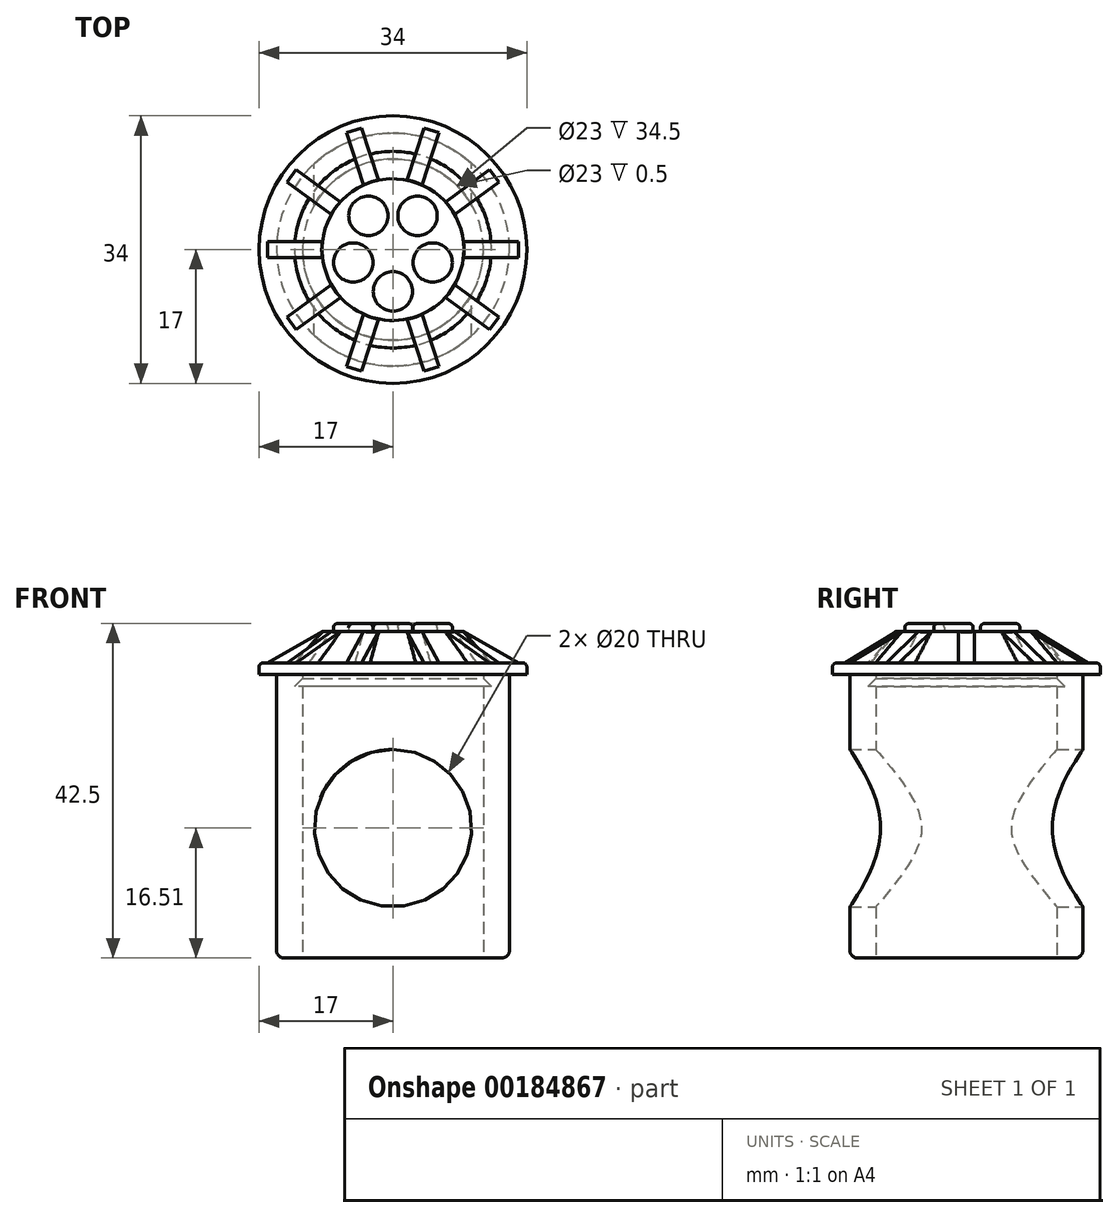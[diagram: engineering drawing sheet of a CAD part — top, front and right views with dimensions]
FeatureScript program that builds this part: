
annotation { "Feature Type Name" : "Feature", "Feature Type Description" : "" }
export const myFeature = defineFeature(function(context is Context, id is Id, definition is map)
    precondition{}
    {
        {
            var Q0;
            Q0=qCreatedBy(makeId("Top.planeOp"),FACE);
            var sketch = newSketch(context, id + "F0", { "sketchPlane" : qUnion([Q0])});
            skCircle(sketch, "E0", {"center": v(0, 0) * mm, "radius": 14.8 * mm});
            skCircle(sketch, "E1", {"center": v(0, 0) * mm, "radius": 11.5 * mm});
            skSolve(sketch);
        }
        {
            var Q0;
            Q0=qSketchRegion(id+"F0",true);
            extrude(context, id + "F1", {"entities" : qUnion([Q0]), "endBound" : BoundingType.SYMMETRIC, "depth" : 36 * mm});
        }
        {
            var Q0;
            Q0=makeQuery(id+"F1.opExtrude","SWEPT_BODY",BODY,{"disambiguationData":[OSD([sQuery(id+"F0.wireOp",EDGE,"E0")])]});
            transform(context, id + "F2", {"entities" : qUnion([Q0]), "transformType" : TransformType.TRANSLATION_3D, "dx" : 0 * mm, "dy" : 0 * mm, "dz" : -23.5 * mm, "makeCopy" : false});
        }
        {
            var Q0;
            Q0=qCreatedBy(makeId("Top.planeOp"),FACE);
            var sketch = newSketch(context, id + "F3", { "sketchPlane" : qUnion([Q0])});
            skCircle(sketch, "E2", {"center": v(0, 0) * mm, "radius": 9 * mm});
            skSolve(sketch);
        }
        {
            var Q0;
            Q0=qSketchRegion(id+"F3",true);
            extrude(context, id + "F4", {"entities" : qUnion([Q0]), "depth" : 4 * mm});
        }
        {
            var Q0;
            Q0=qCreatedBy(makeId("Front.planeOp"),FACE);
            var sketch = newSketch(context, id + "F5", { "sketchPlane" : qUnion([Q0])});
            skLineSegment(sketch, "E3", {"start": v(8.92, 4) * mm, "end": v(8.92, 0) * mm});
            skLineSegment(sketch, "E4", {"start": v(8.92, 0) * mm, "end": v(15.92, 0) * mm});
            skLineSegment(sketch, "E5", {"start": v(15.92, 0) * mm, "end": v(8.92, 4) * mm});
            skSolve(sketch);
        }
        {
            var Q0;
            Q0=qSketchRegion(id+"F5",true);
            extrude(context, id + "F6", {"entities" : qUnion([Q0]), "endBound" : BoundingType.SYMMETRIC, "depth" : 2 * mm});
        }
        {
            var Q0;
            Q0=makeQuery(id+"F6.opExtrude","SWEPT_BODY",BODY,{"disambiguationData":[OSD([sQuery(id+"F5.wireOp",EDGE,"E3"),sQuery(id+"F5.wireOp",EDGE,"E4"),sQuery(id+"F5.wireOp",EDGE,"E5")])]});
            var Q1;
            Q1=makeQuery(id+"F4.opExtrude","SWEPT_FACE",FACE,{"disambiguationData":[OSD([sQuery(id+"F3.wireOp",EDGE,"E2")])]});
            circularPattern(context, id + "F7", {"entities" : qUnion([Q0]), "axis" : qUnion([Q1]), "angle" : 36 * degree, "instanceCount" : 10});
        }
        {
            var Q0;
            Q0=qCreatedBy(makeId("Front.planeOp"),FACE);
            var sketch = newSketch(context, id + "F8", { "sketchPlane" : qUnion([Q0])});
            skLineSegment(sketch, "E6", {"start": v(8.98, 0) * mm, "end": v(8.98, 4) * mm});
            skLineSegment(sketch, "E7", {"start": v(8.98, 4) * mm, "end": v(12.48, 0) * mm});
            skLineSegment(sketch, "E8", {"start": v(12.48, 0) * mm, "end": v(8.98, 0) * mm});
            skSolve(sketch);
        }
        {
            var Q0;
            Q0=qSketchRegion(id+"F8",true);
            var Q1;
            Q1=makeQuery(id+"F4.opExtrude","SWEPT_FACE",FACE,{"disambiguationData":[OSD([sQuery(id+"F3.wireOp",EDGE,"E2")])]});
            revolve(context, id + "F9", {"operationType" : NewBodyOperationType.ADD, "entities" : qUnion([Q0]), "axis" : qUnion([Q1]), "revolveType" : RevolveType.FULL});
        }
        {
            var Q0;
            Q0=makeQuery(id+"F4.opExtrude","SWEPT_BODY",BODY,{"disambiguationData":[OSD([sQuery(id+"F3.wireOp",EDGE,"E2")])]});
            var Q1;
            Q1=makeQuery(id+"F6.opExtrude","SWEPT_BODY",BODY,{"disambiguationData":[OSD([sQuery(id+"F5.wireOp",EDGE,"E3"),sQuery(id+"F5.wireOp",EDGE,"E4"),sQuery(id+"F5.wireOp",EDGE,"E5")])]});
            var Q2;
            Q2=makeQuery(id+"F7.opPattern","COPY",BODY,{"derivedFrom":makeQuery(id+"F6.opExtrude","SWEPT_BODY",BODY,{"disambiguationData":[OSD([sQuery(id+"F5.wireOp",EDGE,"E3"),sQuery(id+"F5.wireOp",EDGE,"E4"),sQuery(id+"F5.wireOp",EDGE,"E5")])]}),"instanceName":"1"});
            var Q3;
            Q3=makeQuery(id+"F7.opPattern","COPY",BODY,{"derivedFrom":makeQuery(id+"F6.opExtrude","SWEPT_BODY",BODY,{"disambiguationData":[OSD([sQuery(id+"F5.wireOp",EDGE,"E3"),sQuery(id+"F5.wireOp",EDGE,"E4"),sQuery(id+"F5.wireOp",EDGE,"E5")])]}),"instanceName":"2"});
            var Q4;
            Q4=makeQuery(id+"F7.opPattern","COPY",BODY,{"derivedFrom":makeQuery(id+"F6.opExtrude","SWEPT_BODY",BODY,{"disambiguationData":[OSD([sQuery(id+"F5.wireOp",EDGE,"E3"),sQuery(id+"F5.wireOp",EDGE,"E4"),sQuery(id+"F5.wireOp",EDGE,"E5")])]}),"instanceName":"3"});
            var Q5;
            Q5=makeQuery(id+"F7.opPattern","COPY",BODY,{"derivedFrom":makeQuery(id+"F6.opExtrude","SWEPT_BODY",BODY,{"disambiguationData":[OSD([sQuery(id+"F5.wireOp",EDGE,"E3"),sQuery(id+"F5.wireOp",EDGE,"E4"),sQuery(id+"F5.wireOp",EDGE,"E5")])]}),"instanceName":"4"});
            var Q6;
            Q6=makeQuery(id+"F7.opPattern","COPY",BODY,{"derivedFrom":makeQuery(id+"F6.opExtrude","SWEPT_BODY",BODY,{"disambiguationData":[OSD([sQuery(id+"F5.wireOp",EDGE,"E3"),sQuery(id+"F5.wireOp",EDGE,"E4"),sQuery(id+"F5.wireOp",EDGE,"E5")])]}),"instanceName":"5"});
            var Q7;
            Q7=makeQuery(id+"F7.opPattern","COPY",BODY,{"derivedFrom":makeQuery(id+"F6.opExtrude","SWEPT_BODY",BODY,{"disambiguationData":[OSD([sQuery(id+"F5.wireOp",EDGE,"E3"),sQuery(id+"F5.wireOp",EDGE,"E4"),sQuery(id+"F5.wireOp",EDGE,"E5")])]}),"instanceName":"6"});
            var Q8;
            Q8=makeQuery(id+"F7.opPattern","COPY",BODY,{"derivedFrom":makeQuery(id+"F6.opExtrude","SWEPT_BODY",BODY,{"disambiguationData":[OSD([sQuery(id+"F5.wireOp",EDGE,"E3"),sQuery(id+"F5.wireOp",EDGE,"E4"),sQuery(id+"F5.wireOp",EDGE,"E5")])]}),"instanceName":"7"});
            var Q9;
            Q9=makeQuery(id+"F7.opPattern","COPY",BODY,{"derivedFrom":makeQuery(id+"F6.opExtrude","SWEPT_BODY",BODY,{"disambiguationData":[OSD([sQuery(id+"F5.wireOp",EDGE,"E3"),sQuery(id+"F5.wireOp",EDGE,"E4"),sQuery(id+"F5.wireOp",EDGE,"E5")])]}),"instanceName":"8"});
            var Q10;
            Q10=makeQuery(id+"F7.opPattern","COPY",BODY,{"derivedFrom":makeQuery(id+"F6.opExtrude","SWEPT_BODY",BODY,{"disambiguationData":[OSD([sQuery(id+"F5.wireOp",EDGE,"E3"),sQuery(id+"F5.wireOp",EDGE,"E4"),sQuery(id+"F5.wireOp",EDGE,"E5")])]}),"instanceName":"9"});
            var Q11;
            Q11=makeQuery(id+"F9.opRevolve","SWEPT_BODY",BODY,{"disambiguationData":[OSD([sQuery(id+"F8.wireOp",EDGE,"E6"),sQuery(id+"F8.wireOp",EDGE,"E7"),sQuery(id+"F8.wireOp",EDGE,"E8")])]});
            transform(context, id + "F10", {"entities" : qUnion([Q0, Q1, Q2, Q3, Q4, Q5, Q6, Q7, Q8, Q9, Q10, Q11]), "transformType" : TransformType.TRANSLATION_3D, "dx" : 0 * mm, "dy" : 0 * mm, "dz" : -4 * mm, "makeCopy" : false});
        }
        {
            var Q0;
            Q0=qCreatedBy(makeId("Top.planeOp"),FACE);
            var sketch = newSketch(context, id + "F11", { "sketchPlane" : qUnion([Q0])});
            skCircle(sketch, "E9", {"center": v(0, -5.3) * mm, "radius": 2.5 * mm});
            skSolve(sketch);
        }
        {
            var Q0;
            Q0=qSketchRegion(id+"F11",true);
            extrude(context, id + "F12", {"entities" : qUnion([Q0]), "depth" : 1 * mm});
        }
        {
            var Q0;
            Q0=makeQuery(id+"F12.opExtrude","CAP_EDGE",EDGE,{"disambiguationData":[OSD([sQuery(id+"F11.wireOp",EDGE,"E9")])],"isStart":false});
            fillet(context, id + "F13", {"entities" : qUnion([Q0]), "radius" : .5 * mm, "tangentPropagation" : true, "allowEdgeOverflow" : false});
        }
        {
            var Q0;
            Q0=makeQuery(id+"F12.opExtrude","SWEPT_BODY",BODY,{"disambiguationData":[OSD([sQuery(id+"F11.wireOp",EDGE,"E9")])]});
            var Q1;
            Q1=makeQuery(id+"F4.opExtrude","SWEPT_FACE",FACE,{"disambiguationData":[OSD([sQuery(id+"F3.wireOp",EDGE,"E2")])]});
            circularPattern(context, id + "F14", {"entities" : qUnion([Q0]), "axis" : qUnion([Q1]), "angle" : 72 * degree, "instanceCount" : 5});
        }
        {
            var Q0;
            Q0=qCreatedBy(makeId("Top.planeOp"),FACE);
            var sketch = newSketch(context, id + "F15", { "sketchPlane" : qUnion([Q0])});
            skCircle(sketch, "E10", {"center": v(0, 0) * mm, "radius": 17 * mm});
            skSolve(sketch);
        }
        {
            var Q0;
            Q0=qSketchRegion(id+"F15",true);
            extrude(context, id + "F16", {"entities" : qUnion([Q0]), "depth" : 1.5 * mm});
        }
        {
            var Q0;
            Q0=makeQuery(id+"F16.opExtrude","CAP_EDGE",EDGE,{"disambiguationData":[OSD([sQuery(id+"F15.wireOp",EDGE,"E10")])],"isStart":false});
            fillet(context, id + "F17", {"entities" : qUnion([Q0]), "radius" : .5 * mm, "tangentPropagation" : true, "allowEdgeOverflow" : false});
        }
        {
            var Q0;
            Q0=makeQuery(id+"F16.opExtrude","SWEPT_BODY",BODY,{"disambiguationData":[OSD([sQuery(id+"F15.wireOp",EDGE,"E10")])]});
            transform(context, id + "F18", {"entities" : qUnion([Q0]), "transformType" : TransformType.TRANSLATION_3D, "dx" : 0 * mm, "dy" : 0 * mm, "dz" : -5.5 * mm, "makeCopy" : false});
        }
        {
            var Q0;
            Q0=qCreatedBy(makeId("Front.planeOp"),FACE);
            var sketch = newSketch(context, id + "F19", { "sketchPlane" : qUnion([Q0])});
            skLineSegment(sketch, "E11", {"start": v(16.79, -5.5) * mm, "end": v(14.79, -5.5) * mm});
            skLineSegment(sketch, "E12", {"start": v(14.79, -5.5) * mm, "end": v(14.79, -7.5) * mm});
            skArc(sketch, "E13", {"start": v(16.79, -5.5) * mm, "mid": v(15.37, -6.08) * mm, "end": v(14.79, -7.5) * mm});
            skSolve(sketch);
        }
        {
            var Q0;
            Q0 = qConstructionFilter(qBodyType(qCreatedBy(id + "F19" ,EDGE), BodyType.WIRE), ConstructionObject.NO);
            var Q1;
            Q1=makeQuery(id+"F1.opExtrude","SWEPT_FACE",FACE,{"disambiguationData":[OSD([sQuery(id+"F0.wireOp",EDGE,"E0")])]});
            revolve(context, id + "F20", {"bodyType" : ToolBodyType.SURFACE, "surfaceEntities" : qUnion([Q0]), "axis" : qUnion([Q1]), "revolveType" : RevolveType.FULL});
        }
        {
            var Q0;
            Q0=qCreatedBy(makeId("Top.planeOp"),FACE);
            var sketch = newSketch(context, id + "F21", { "sketchPlane" : qUnion([Q0])});
            skCircle(sketch, "E14", {"center": v(0, 0) * mm, "radius": 12.5 * mm});
            skSolve(sketch);
        }
        {
            var Q0;
            Q0 = qSketchRegion(id + "F21", true);
            extrude(context, id + "F22", {"entities" : qUnion([Q0]), "oppositeDirection" : true, "depth" : 5 * mm});
        }
        {
            var Q0;
            Q0=makeQuery(id+"F22.opExtrude","CAP_EDGE",EDGE,{"disambiguationData":[OSD([sQuery(id+"F21.wireOp",EDGE,"E14")])],"isStart":true});
            chamfer(context, id + "F23", {"entities" : qUnion([Q0]), "chamferType" : ChamferType.TWO_OFFSETS, "width1" : 5 * mm, "oppositeDirection" : false, "width2" : 5 * mm, "tangentPropagation" : true});
        }
        {
            var Q0;
            Q0=makeQuery(id+"F22.opExtrude","SWEPT_BODY",BODY,{"disambiguationData":[OSD([sQuery(id+"F21.wireOp",EDGE,"E14")])]});
            transform(context, id + "F24", {"entities" : qUnion([Q0]), "transformType" : TransformType.TRANSLATION_3D, "dx" : 0 * mm, "dy" : 0 * mm, "dz" : -2 * mm, "makeCopy" : false});
        }
        {
            var Q0;
            Q0=qCreatedBy(makeId("Front.planeOp"),FACE);
            var sketch = newSketch(context, id + "F25", { "sketchPlane" : qUnion([Q0])});
            skEllipse(sketch, "E15", {"center": v(0, -25) * mm, "majorRadius": 10 * mm, "minorRadius": 10 * mm, "majorAxis": v(0, -1)});
            skSolve(sketch);
        }
        {
            var Q0;
            Q0 = qSketchRegion(id + "F25", true);
            extrude(context, id + "F26", {"entities" : qUnion([Q0]), "endBound" : BoundingType.SYMMETRIC, "depth" : 40 * mm});
        }
        {
            var Q0;
            Q0=makeQuery(id+"F22.opExtrude","SWEPT_BODY",BODY,{"disambiguationData":[OSD([sQuery(id+"F21.wireOp",EDGE,"E14")])]});
            var Q1;
            Q1=makeQuery(id+"F26.opExtrude","SWEPT_BODY",BODY,{"disambiguationData":[OSD([sQuery(id+"F25.wireOp",EDGE,"E15")])]});
            var Q2;
            Q2=makeQuery(id+"F1.opExtrude","SWEPT_BODY",BODY,{"disambiguationData":[OSD([sQuery(id+"F0.wireOp",EDGE,"E0"),sQuery(id+"F0.wireOp",EDGE,"E1")])]});
            booleanBodies(context, id + "F27", {"operationType" : BooleanOperationType.SUBTRACTION, "tools" : qUnion([Q0, Q1]), "targets" : qUnion([Q2])});
        }
        {
            var Q0;
            Q0=makeQuery(id+"F1.opExtrude","CAP_EDGE",EDGE,{"disambiguationData":[OSD([sQuery(id+"F0.wireOp",EDGE,"E0")])],"isStart":true});
            fillet(context, id + "F28", {"entities" : qUnion([Q0]), "radius" : 1 * mm, "tangentPropagation" : true, "allowEdgeOverflow" : false});
        }
    });
